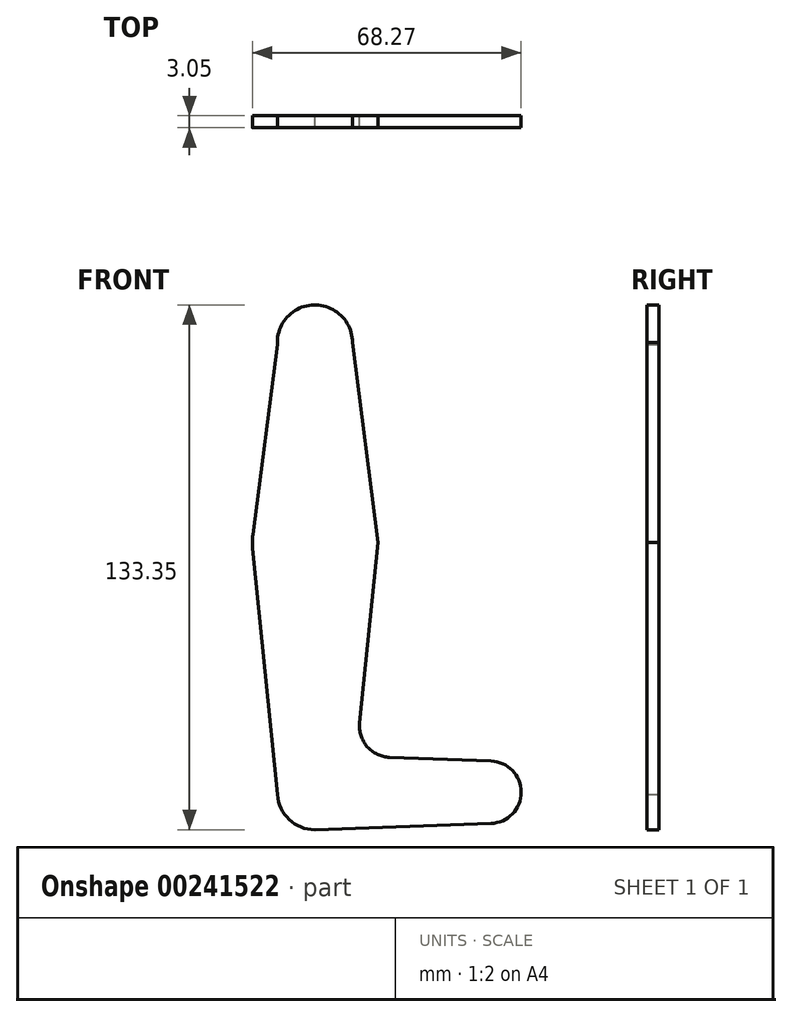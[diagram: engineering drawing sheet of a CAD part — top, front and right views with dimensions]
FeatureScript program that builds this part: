
annotation { "Feature Type Name" : "Feature", "Feature Type Description" : "" }
export const myFeature = defineFeature(function(context is Context, id is Id, definition is map)
    precondition{}
    {
        {
            var Q0;
            Q0=qCreatedBy(makeId("Front.planeOp"),FACE);
            var sketch = newSketch(context, id + "F0", { "sketchPlane" : qUnion([Q0])});
            skLineSegment(sketch, "E0", {"start": v(0, 0) * mm, "end": v(0, 50.8) * mm, "construction": true});
            skLineSegment(sketch, "E1", {"start": v(0, 0) * mm, "end": v(0, -63.5) * mm, "construction": true});
            skLineSegment(sketch, "E2", {"start": v(0, -63.5) * mm, "end": v(44.45, -63.5) * mm, "construction": true});
            skCircle(sketch, "E3", {"center": v(0, 50.8) * mm, "radius": 9.53 * mm});
            skCircle(sketch, "E4", {"center": v(0, 0) * mm, "radius": 15.88 * mm});
            skCircle(sketch, "E5", {"center": v(44.45, -63.5) * mm, "radius": 7.94 * mm});
            skCircle(sketch, "E6", {"center": v(0, -63.5) * mm, "radius": 9.53 * mm});
            skLineSegment(sketch, "E7", {"start": v(-9.5, 50.25) * mm, "end": v(-16, 0) * mm});
            skLineSegment(sketch, "E8", {"start": v(-9.5, -64.1) * mm, "end": v(-15.8, -1.59) * mm});
            skLineSegment(sketch, "E9", {"start": v(9.53, 50.8) * mm, "end": v(16, 0) * mm});
            skLineSegment(sketch, "E10", {"start": v(0, -73.03) * mm, "end": v(44.73, -71.43) * mm});
            skLineSegment(sketch, "E11", {"start": v(44.73, -55.57) * mm, "end": v(19, -54.65) * mm});
            skLineSegment(sketch, "E12", {"start": v(16, 0) * mm, "end": v(11.38, -45.9) * mm});
            skPoint(sketch, "E13.visualSharp", {"position": v(10.53, -54.35) * mm});
            skArc(sketch, "E13.filletArc", {"start": v(11.38, -45.9) * mm, "mid": v(13.3, -51.93) * mm, "end": v(19, -54.65) * mm});
            skSolve(sketch);
        }
        {
            var Q0;
            {var subQ0=sQuery(id+"F0.wireOp",EDGE,"E3");var subQ1=makeQuery(id+"F0.imprint","INTERSECT",VERTEX,{"derivedFrom":[subQ0,sQuery(id+"F0.wireOp",EDGE,"E7")]});Q0=makeQuery(id+"F0.imprint","IMPRINT",FACE,{"disambiguationData":[TD([[makeQuery(id+"F0.imprint","IMPRINT",EDGE,{"disambiguationData":[TD([[subQ1,1.0]])],"derivedFrom":subQ0}),1.0]])]});}
            var Q1;
            {var subQ0=sQuery(id+"F0.wireOp",EDGE,"E7");var subQ1=sQuery(id+"F0.wireOp",EDGE,"E3");var subQ2=makeQuery(id+"F0.imprint","INTERSECT",VERTEX,{"derivedFrom":[subQ1,subQ0]});Q1=makeQuery(id+"F0.imprint","IMPRINT",FACE,{"disambiguationData":[TD([[makeQuery(id+"F0.imprint","IMPRINT",EDGE,{"disambiguationData":[TD([[subQ2,-1.0]])],"derivedFrom":subQ1}),-1.0]])]});}
            var Q2;
            {var subQ0=sQuery(id+"F0.wireOp",EDGE,"E4");var subQ1=makeQuery(id+"F0.imprint","INTERSECT",VERTEX,{"derivedFrom":[subQ0,sQuery(id+"F0.wireOp",EDGE,"E7")]});Q2=makeQuery(id+"F0.imprint","IMPRINT",FACE,{"disambiguationData":[TD([[makeQuery(id+"F0.imprint","IMPRINT",EDGE,{"disambiguationData":[TD([[subQ1,1.0]])],"derivedFrom":subQ0}),1.0]])]});}
            var Q3;
            {var subQ0=sQuery(id+"F0.wireOp",EDGE,"E8");Q3=makeQuery(id+"F0.imprint","IMPRINT",FACE,{"disambiguationData":[TD([[makeQuery(id+"F0.imprint","IMPRINT",EDGE,{"derivedFrom":subQ0}),-1.0]])]});}
            var Q4;
            {var subQ0=sQuery(id+"F0.wireOp",EDGE,"E6");var subQ1=makeQuery(id+"F0.imprint","INTERSECT",VERTEX,{"derivedFrom":[subQ0,sQuery(id+"F0.wireOp",EDGE,"E8")]});Q4=makeQuery(id+"F0.imprint","IMPRINT",FACE,{"disambiguationData":[TD([[makeQuery(id+"F0.imprint","IMPRINT",EDGE,{"disambiguationData":[TD([[subQ1,-1.0]])],"derivedFrom":subQ0}),1.0]])]});}
            var Q5;
            {var subQ0=sQuery(id+"F0.wireOp",EDGE,"E5");var subQ1=makeQuery(id+"F0.imprint","INTERSECT",VERTEX,{"derivedFrom":[subQ0,sQuery(id+"F0.wireOp",EDGE,"E10")]});Q5=makeQuery(id+"F0.imprint","IMPRINT",FACE,{"disambiguationData":[TD([[makeQuery(id+"F0.imprint","IMPRINT",EDGE,{"disambiguationData":[TD([[subQ1,1.0]])],"derivedFrom":subQ0}),1.0]])]});}
            extrude(context, id + "F1", {"entities" : qUnion([Q0, Q1, Q2, Q3, Q4, Q5]), "depth" : 3.05 * mm});
        }
    });
